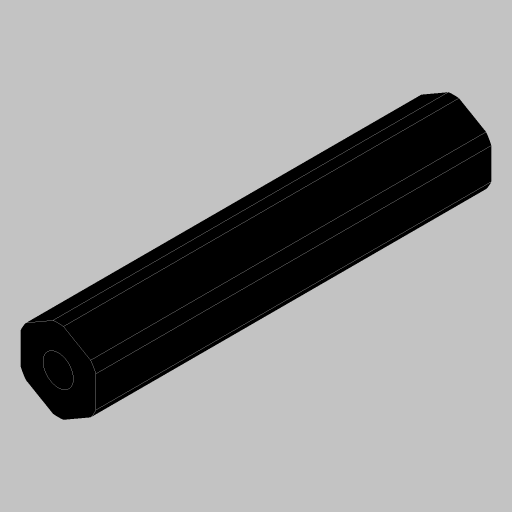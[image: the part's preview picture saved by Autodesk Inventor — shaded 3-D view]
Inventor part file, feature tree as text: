
AUTODESK INVENTOR PART (.ipt)
format: ipt  version: 2023.5 (Build 275446000, 446)  size: 120,320 bytes
history: native  units: in
note: dims shown in document units (in); Inventor stores cm internally (conversion verified against a paired STEP export)
features: extrude x2, projected_geometry x2, hole x1
ambient origin geometry x8: Origin, YZ Plane, XZ Plane, XY Plane, X Axis, Y Axis, Z Axis, Center Point
bodies: Solid1 (feature_tree)
feature tree (5):
  extrude  "Extrusion1"  TaperAngle=0.0deg  [1 undecoded]
  hole  "Hole1"  [1 undecoded]
  extrude  "Extrusion3"  TaperAngle=0.0deg  [1 undecoded]
  projected_geometry  "Project Cut Edges1"
  projected_geometry  "Project Cut Edges2"
note: 3 required parameter values undecoded (feature->parameter linkage not recoverable at this tier; creation-order binding heuristic only, values carry confidence <= 0.55)
